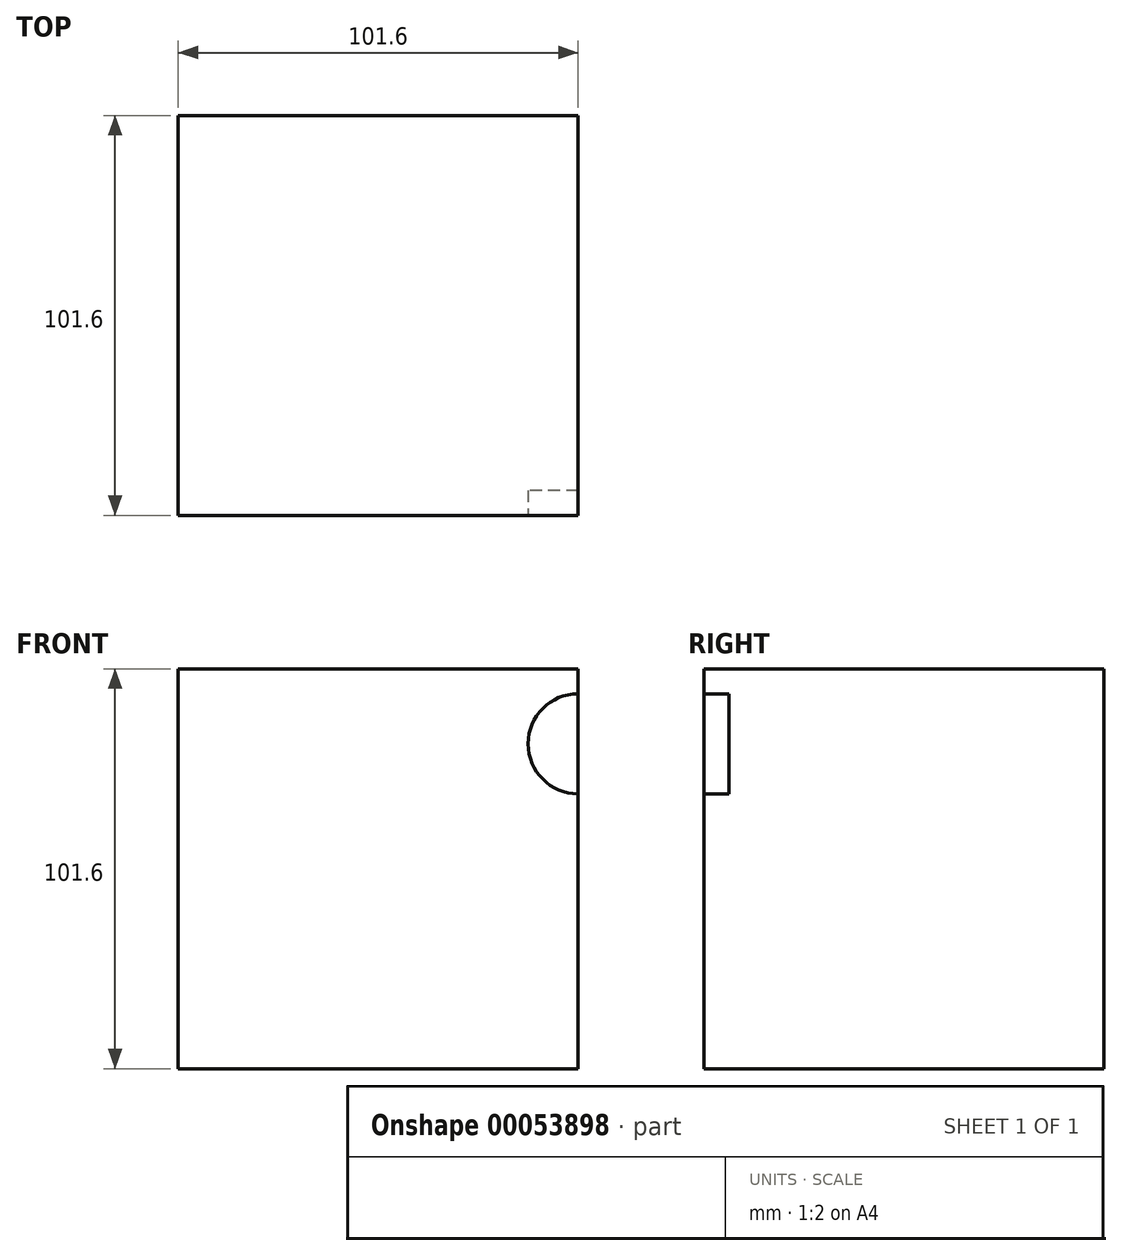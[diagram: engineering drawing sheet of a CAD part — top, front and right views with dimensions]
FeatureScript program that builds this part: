
annotation { "Feature Type Name" : "Feature", "Feature Type Description" : "" }
export const myFeature = defineFeature(function(context is Context, id is Id, definition is map)
    precondition{}
    {
        {
            var Q0;
            Q0=qCreatedBy(makeId("Front.planeOp"),FACE);
            var sketch = newSketch(context, id + "F0", { "sketchPlane" : qUnion([Q0])});
            skLineSegment(sketch, "E0.rect.bottom", {"start": v(-50.8, 50.8) * mm, "end": v(50.8, 50.8) * mm});
            skLineSegment(sketch, "E0.rect.top", {"start": v(-50.8, -50.8) * mm, "end": v(50.8, -50.8) * mm});
            skLineSegment(sketch, "E0.rect.left", {"start": v(-50.8, 50.8) * mm, "end": v(-50.8, -50.8) * mm});
            skLineSegment(sketch, "E0.rect.right", {"start": v(50.8, 50.8) * mm, "end": v(50.8, -50.8) * mm});
            skPoint(sketch, "E0.rect.middle", {"position": v(0, 0) * mm});
            skSolve(sketch);
        }
        {
            var Q0;
            Q0 = qSketchRegion(id + "F0", true);
            extrude(context, id + "F1", {"entities" : qUnion([Q0]), "endBound" : BoundingType.SYMMETRIC, "depth" : 101.6 * mm});
        }
        {
            var Q0;
            Q0=makeQuery(id+"F1.opExtrude","CAP_FACE",FACE,{"disambiguationData":[OSD([sQuery(id+"F0.wireOp",EDGE,"E0.rect.bottom"),sQuery(id+"F0.wireOp",EDGE,"E0.rect.top"),sQuery(id+"F0.wireOp",EDGE,"E0.rect.left"),sQuery(id+"F0.wireOp",EDGE,"E0.rect.right")])],"isStart":false});
            var sketch = newSketch(context, id + "F2", { "sketchPlane" : qUnion([Q0])});
            skCircle(sketch, "E1", {"center": v(50.8, 31.75) * mm, "radius": 12.7 * mm});
            skSolve(sketch);
        }
        {
            var Q0;
            Q0 = qSketchRegion(id + "F2", true);
            extrude(context, id + "F3", {"entities" : qUnion([Q0]), "operationType" : NewBodyOperationType.REMOVE, "oppositeDirection" : true, "depth" : 6.35 * mm});
        }
    });
